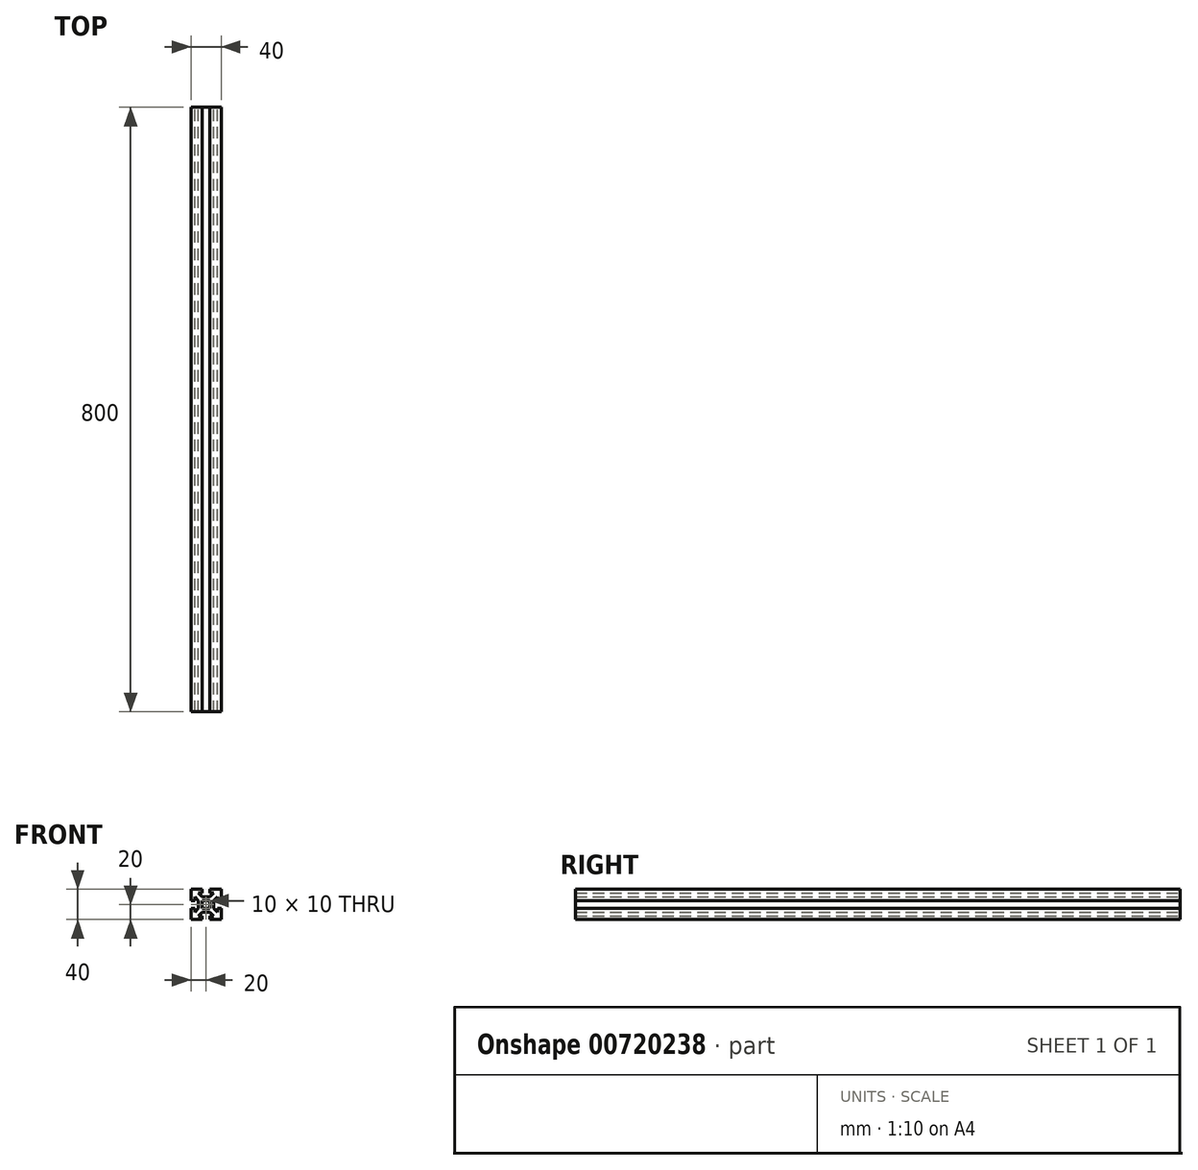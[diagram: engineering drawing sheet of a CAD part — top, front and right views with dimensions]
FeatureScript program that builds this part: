
annotation { "Feature Type Name" : "Feature", "Feature Type Description" : "" }
export const myFeature = defineFeature(function(context is Context, id is Id, definition is map)
    precondition{}
    {
        {
            var Q0;
            Q0=qCreatedBy(makeId("Front.planeOp"),FACE);
            var sketch = newSketch(context, id + "F0", { "sketchPlane" : qUnion([Q0])});
            skLineSegment(sketch, "E0.bottom", {"start": v(20, 20) * mm, "end": v(5, 20) * mm});
            skLineSegment(sketch, "E0.top", {"start": v(20, -20) * mm, "end": v(5, -20) * mm});
            skLineSegment(sketch, "E0.left", {"start": v(20, 20) * mm, "end": v(20, 5) * mm});
            skLineSegment(sketch, "E0.right", {"start": v(-20, 20) * mm, "end": v(-20, 5) * mm});
            skPoint(sketch, "E0.middle", {"position": v(0, 0) * mm});
            skLineSegment(sketch, "E1", {"start": v(0, 20) * mm, "end": v(0, -20) * mm, "construction": true});
            skLineSegment(sketch, "E2", {"start": v(-20, 0) * mm, "end": v(20, 0) * mm, "construction": true});
            skLineSegment(sketch, "E3", {"start": v(-20, 5) * mm, "end": v(-15, 5) * mm});
            skLineSegment(sketch, "E4", {"start": v(-20, -5) * mm, "end": v(-15, -5) * mm});
            skLineSegment(sketch, "E5", {"start": v(-5, 20) * mm, "end": v(-5, 15) * mm});
            skLineSegment(sketch, "E6", {"start": v(5, 20) * mm, "end": v(5, 15) * mm});
            skLineSegment(sketch, "E7", {"start": v(-10, 15) * mm, "end": v(-5, 15) * mm});
            skLineSegment(sketch, "E8", {"start": v(-10, -15) * mm, "end": v(-5, -15) * mm});
            skLineSegment(sketch, "E9", {"start": v(15, 10) * mm, "end": v(15, 5) * mm});
            skLineSegment(sketch, "E10", {"start": v(-15, 10) * mm, "end": v(-10, 5) * mm});
            skLineSegment(sketch, "E11", {"start": v(-10, 15) * mm, "end": v(-5, 10) * mm});
            skLineSegment(sketch, "E12", {"start": v(-15, -10) * mm, "end": v(-10, -5) * mm});
            skLineSegment(sketch, "E13", {"start": v(-10, -15) * mm, "end": v(-5, -10) * mm});
            skLineSegment(sketch, "E14.trimOffspring", {"start": v(20, -5) * mm, "end": v(20, -20) * mm});
            skLineSegment(sketch, "E15.trimOffspring", {"start": v(-20, -5) * mm, "end": v(-20, -20) * mm});
            skLineSegment(sketch, "E16.trimOffspring", {"start": v(-5, -20) * mm, "end": v(-20, -20) * mm});
            skLineSegment(sketch, "E17.trimOffspring", {"start": v(-5, 20) * mm, "end": v(-20, 20) * mm});
            skLineSegment(sketch, "E18.trimOffspring", {"start": v(5, 15) * mm, "end": v(10, 15) * mm});
            skLineSegment(sketch, "E19.trimOffspring", {"start": v(-15, -5) * mm, "end": v(-15, -10) * mm});
            skLineSegment(sketch, "E20.trimOffspring", {"start": v(15, -5) * mm, "end": v(15, -10) * mm});
            skLineSegment(sketch, "E21.trimOffspring", {"start": v(5, -15) * mm, "end": v(10, -15) * mm});
            skLineSegment(sketch, "E22.trimOffspring", {"start": v(-5, 5) * mm, "end": v(-5, -5) * mm});
            skLineSegment(sketch, "E23.trimOffspring", {"start": v(5, 5) * mm, "end": v(5, -5) * mm});
            skLineSegment(sketch, "E24.trimOffspring", {"start": v(15, 5) * mm, "end": v(20, 5) * mm});
            skLineSegment(sketch, "E25.trimOffspring", {"start": v(15, -5) * mm, "end": v(20, -5) * mm});
            skLineSegment(sketch, "E26.trimOffspring", {"start": v(5, -15) * mm, "end": v(5, -20) * mm});
            skLineSegment(sketch, "E27.trimOffspring", {"start": v(-5, -15) * mm, "end": v(-5, -20) * mm});
            skLineSegment(sketch, "E28.trimOffspring", {"start": v(-5, -5) * mm, "end": v(5, -5) * mm});
            skLineSegment(sketch, "E29.trimOffspring", {"start": v(-5, 5) * mm, "end": v(5, 5) * mm});
            skLineSegment(sketch, "E30", {"start": v(10, 5) * mm, "end": v(10, -5) * mm});
            skLineSegment(sketch, "E31", {"start": v(-5, 10) * mm, "end": v(5, 10) * mm});
            skLineSegment(sketch, "E32", {"start": v(-10, 5) * mm, "end": v(-10, -5) * mm});
            skLineSegment(sketch, "E33", {"start": v(-5, -10) * mm, "end": v(5, -10) * mm});
            skLineSegment(sketch, "E34.trimOffspring", {"start": v(-15, 10) * mm, "end": v(-15, 5) * mm});
            skPoint(sketch, "E35.orphan", {"position": v(20, 15) * mm});
            skPoint(sketch, "E36.orphan", {"position": v(20, -15) * mm});
            skPoint(sketch, "E37.orphan", {"position": v(15, -20) * mm});
            skPoint(sketch, "E38.orphan", {"position": v(-15, -20) * mm});
            skLineSegment(sketch, "E39.trimOffspring", {"start": v(-5, 0) * mm, "end": v(0, -5) * mm});
            skLineSegment(sketch, "E40.trimOffspring", {"start": v(-5, 0) * mm, "end": v(0, 5) * mm});
            skLineSegment(sketch, "E41.trimOffspring", {"start": v(0, 5) * mm, "end": v(5, 0) * mm});
            skLineSegment(sketch, "E42.trimOffspring", {"start": v(5, 10) * mm, "end": v(10, 15) * mm});
            skLineSegment(sketch, "E43.trimOffspring", {"start": v(10, 5) * mm, "end": v(15, 10) * mm});
            skLineSegment(sketch, "E44.trimOffspring", {"start": v(10, -5) * mm, "end": v(15, -10) * mm});
            skLineSegment(sketch, "E45.trimOffspring", {"start": v(5, -10) * mm, "end": v(10, -15) * mm});
            skLineSegment(sketch, "E46.trimOffspring", {"start": v(0, -5) * mm, "end": v(5, 0) * mm});
            skSolve(sketch);
        }
        {
            var Q0;
            Q0=makeQuery(id+"F0.imprint","IMPRINT",FACE,{"disambiguationData":[TD([[makeQuery(id+"F0.imprint","IMPRINT",EDGE,{"derivedFrom":sQuery(id+"F0.wireOp",EDGE,"E0.bottom")}),1.0]])]});
            extrude(context, id + "F1", {"entities" : qUnion([Q0]), "depth" : 800 * mm, "offsetDistance" : 25 * mm});
        }
    });
